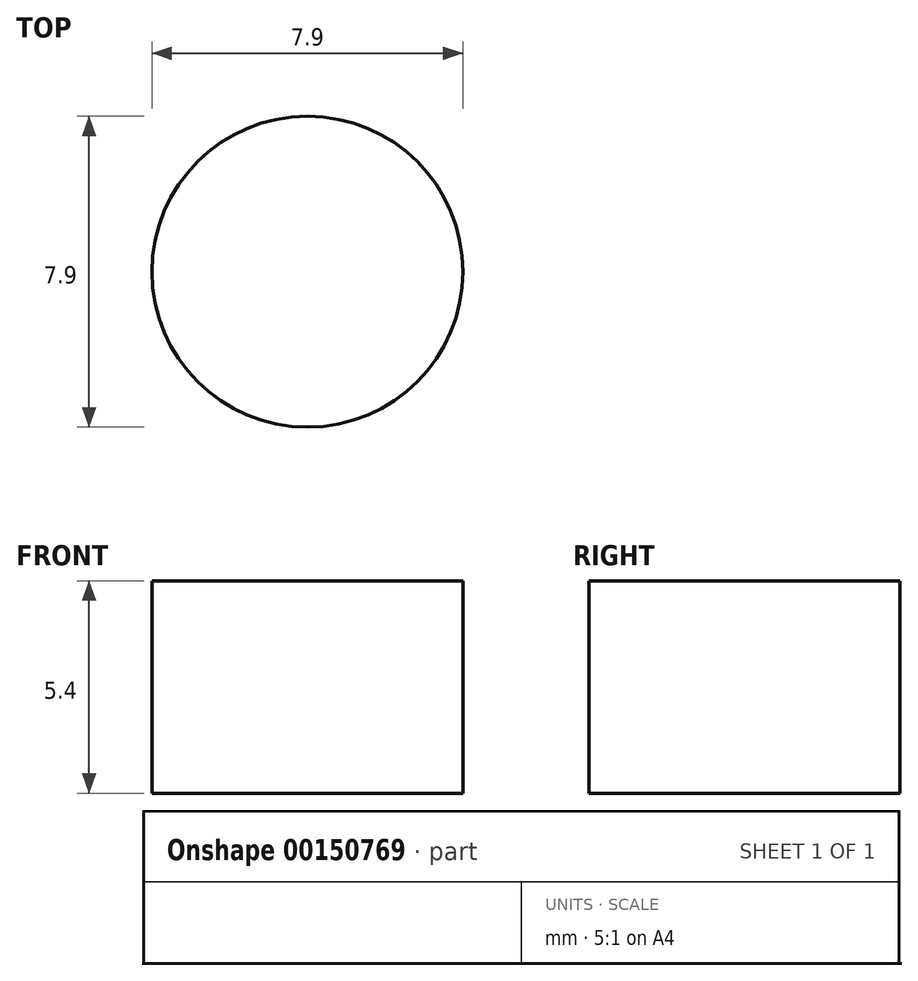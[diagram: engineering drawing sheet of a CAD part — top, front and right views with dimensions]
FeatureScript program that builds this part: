
annotation { "Feature Type Name" : "Feature", "Feature Type Description" : "" }
export const myFeature = defineFeature(function(context is Context, id is Id, definition is map)
    precondition{}
    {
        {
            var Q0;
            Q0=qCreatedBy(makeId("Top.planeOp"),FACE);
            var sketch = newSketch(context, id + "F0", { "sketchPlane" : qUnion([Q0])});
            skCircle(sketch, "E0", {"center": v(0, 0) * mm, "radius": 3.95 * mm});
            skSolve(sketch);
        }
        {
            var Q0;
            Q0 = qSketchRegion(id + "F0", true);
            extrude(context, id + "F1", {"entities" : qUnion([Q0]), "depth" : 5.4 * mm});
        }
    });
